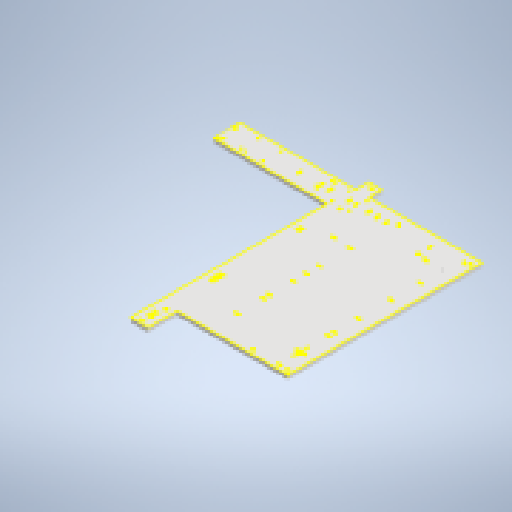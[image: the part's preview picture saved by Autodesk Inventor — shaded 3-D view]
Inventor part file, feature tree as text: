
AUTODESK INVENTOR PART (.ipt)
format: ipt  version: 2025.2 (Build 292293000, 293)  size: 1,572,352 bytes
history: native  units: in
note: dims shown in document units (in); Inventor stores cm internally (conversion verified against a paired STEP export)
features: extrude x26, other x16, sketch x11, hole x5, projected_geometry x4, move_body x3, plane x1, direct_edit x1
ambient origin geometry x8: Origin, YZ Plane, XZ Plane, XY Plane, X Axis, Y Axis, Z Axis, Center Point
bodies: Solid1 (feature_tree)
feature tree (67):
  other  "BoardMounting"
  plane  "Work Plane1"
  sketch  "Sketch2"  dims[d0=0.5in d1=0.5in]
  extrude  "Extrusion4"  Depth=0.5in
  extrude  "ForwardPathDowellPins"  Depth=0.25in
  extrude  "ReversePathDowellPins"  Depth=36.76in
  other  "CTASLMHoles"
  other  "VCSection"
  extrude  "VCPlate"  Depth=0.25in
  hole  "Hole1"  [1 undecoded]
  other  "BaseplateMountingHoles"
  extrude  "BaseplateMountingHolesInner"  Depth=3.175in
  extrude  "BaseplateMountingHolesOuter"  Depth=2.76in
  extrude  "CTASLMElementHolesTop"  Depth=2.577in
  extrude  "Extrusion10"  Depth=7.4961in
  extrude  "Extrusion11"  Depth=1.5in
  sketch  "Sketch8"  dims[d2=0.25in d3=0.4in]
  other  "CylindricalPath"
  other  "CylindricalPathOption1"
  other  "CylindricalPathOption2"
  other  "CylindricalPathOption3"
  other  "CylindricalPathOption3_CTaslmHoles"
  hole  "Hole2"  [1 undecoded]
  extrude  "Extrusion12"  Depth=0.25in
  other  "CylindricalPathOption4"
  hole  "Hole3"  [1 undecoded]
  other  "CylindricalPathOption4_CTaslmHoles"
  extrude  "Extrusion13"  Depth=0.25in
  direct_edit  "Direct Edit1"
  extrude  "CPO4_InnerHolesASLM"  Depth=0.25in
  extrude  "CPO4_InnerHolesCTASLM"  Depth=1.5in
  extrude  "CPO4_OuterHoles"  Depth=0.25in
  extrude  "CPO4_DowellPinsASLM"  Depth=1.5in
  extrude  "CPO4_DowelPinsCTASLM"  Depth=0.25in
  sketch  "Sketch22"  dims[d11=1.5in d12=0.5in]
  extrude  "Extrusion19"  Depth=0.25in
  extrude  "Extrusion20"  Depth=0.25in
  extrude  "Extrusion21"  Depth=0.5in
  extrude  "Extrusion22"  Depth=0.25in
  sketch  "Sketch24"  dims[d15=0.665in d16=2.76in]
  other  "Additional Alignment Holes Top"
  hole  "Hole4"  [1 undecoded]
  extrude  "Extrusion23"  Depth=0.25in
  extrude  "Extrusion24"  Depth=0.25in
  extrude  "Extrusion25"  Depth=0.25in
  sketch  "Sketch27"  dims[d19=10.479in d20=7.4961in]
  extrude  "Extrusion26"  Depth=0.25in
  extrude  "Extrusion27"  Depth=0.25in
  extrude  "Extrusion28"  Depth=0.25in
  hole  "Hole5"  [1 undecoded]
  sketch  "Sketch29"  dims[d23=2.0in d24=0.25in d25=0.197in d26=0.197in d27=0.0797in d28=0.0797in d29=0.25in d30=0.197in d31=0.197in d32=0.0797in d33=0.0797in d34=0.25in d35=0.197in d36=0.197in d37=0.0797in d38=0.0797in d39=0.25in d40=0.197in d41=0.197in d42=0.0797in d43=0.0797in d44=0.25in d45=0.197in d46=0.197in d47=0.0797in d48=0.0797in d49=0.25in d50=0.197in d51=0.197in d52=0.0797in d53=0.0797in d54=0.25in d55=0.197in d56=0.197in d57=0.0797in d58=0.0797in d59=0.25in d60=0.197in d61=0.197in d62=0.0797in d63=0.0797in d64=0.25in d65=0.197in d66=0.197in d67=0.08in d68=0.08in d69=0.25in d70=0.197in d71=0.197in d72=0.08in d73=0.08in d74=0.25in d75=0.197in d76=0.197in d77=0.08in d78=0.08in d81=0.175in d82=0.0in d83=1.5in d84=8.979in d85=1.5in d86=7.4961in d87=6.021in d88=1.0in d89=0.5in d90=0.4738in d91=0.4738in d92=0.25in d93=0.0797in d94=0.0797in d95=0.4738in d96=0.4738in d97=0.25in d98=0.0797in d99=0.0797in d100=0.25in d101=0.197in d102=0.197in d103=0.0797in d104=0.0797in d105=0.25in d106=0.197in d107=0.197in d108=0.0797in d109=0.0797in d110=0.25in d111=0.197in d112=0.0797in d113=0.0797in d114=0.25in d115=0.197in d116=0.0797in d117=0.0797in d118=0.5in d119=1.5in d120=0.5in d121=0.0in d122=0.75in d123=4.857in d124=9.8971in d125=6.8583in d126=1.5in d127=1.5in d128=0.5in d129=1.5in d130=0.25in d131=0.197in d132=0.197in d133=0.0797in d134=0.0797in d135=0.25in d136=0.197in d137=0.197in d138=0.0797in d139=0.0797in d140=0.25in d141=0.197in d142=0.197in d143=0.0797in d144=0.0797in d145=0.175in d146=0.0in d147=9.1809in d148=7.0827in d149=0.25in d150=0.197in d151=0.197in d152=0.0797in d153=0.0797in d154=0.25in d155=0.197in d156=0.197in d157=0.0797in d158=0.0797in d160=0.8752in d161=3.0276in d162=0.1061in d163=0.19in d164=1.5in d165=2.0in d166=1.0in d167=1.0in d168=1.0in d169=0.6in d170=0.5in d171=0.0in d172=0.196in d173=0.5in d174=0.375in d175=0.25in d176=0.5635in d177=1.0in d178=0.8108in d179=21.0in d180=27.0in d181=2.0in d182=14.0in d183=20.0in d184=2.0in d185=19.0in d186=0.4in d187=0.25in d188=0.4in d189=0.25in d190=0.4in d191=0.25in d192=0.4in d193=0.25in d194=0.4in d195=0.25in d196=0.4in d197=0.25in d198=0.4in d199=0.25in d200=0.4in d201=0.25in d202=0.4in d203=0.25in d204=0.4in d205=0.25in d206=0.5in d207=0.0in d208=0.3in d209=0.0in d210=2.0in d211=0.0in d212=0.175in d213=0.0in d214=0.4in d215=0.4in d216=0.4in d217=0.4in d218=0.4in d219=0.4in d220=0.4in d221=0.4in d222=0.4in d223=0.4in d224=0.4in d225=0.4in d226=0.4in d227=0.4in d228=0.4in d229=0.4in d230=0.4in d231=0.4in d232=0.4in d233=0.3in d234=0.0in d235=3.7433in d236=0.25in d237=0.0797in d238=0.0797in d239=0.4in d240=2.5in d241=0.75in d242=0.25in d243=0.0797in d244=0.0797in d245=1.0in d246=1.0in d247=9.1809in d248=7.0827in d249=0.25in d250=0.197in d251=0.197in d252=0.0797in d253=0.0797in d254=0.25in d255=0.197in d256=0.197in d257=0.0797in d258=0.0797in d264=0.25in d265=0.197in d266=0.197in d267=0.0797in d268=0.0797in d269=1.0in d270=1.0in d271=9.8971in d272=6.8583in d273=0.5in d274=1.5in d275=0.25in d276=0.197in d277=0.197in d278=0.0797in d279=0.0797in d280=0.25in d281=0.197in d282=0.197in d283=0.0797in d284=0.0797in d285=0.25in d286=0.197in d287=0.197in d288=0.0797in d289=0.0797in d290=1.0in d291=0.4in d292=0.4in d293=0.4in d294=0.4in d295=0.4in d296=0.4in d297=1.5in d298=0.5in d299=3.0in d300=0.6736in d301=2.7622in d302=1.5in d303=1.5in d304=3.6673in d305=6.9909in d306=1.5in d307=3.9528in d308=0.197in d309=0.197in d310=0.08in d311=0.08in d312=0.25in d313=0.197in d314=0.197in d315=0.08in d316=0.08in d317=0.25in d318=0.197in d319=0.197in d320=0.08in d321=0.08in d322=0.25in d323=0.197in d324=0.197in d325=0.08in d326=0.08in d327=0.25in d328=0.197in d329=0.197in d330=0.08in d331=0.08in d332=0.25in d333=0.197in d334=0.197in d335=0.08in d336=0.08in d337=0.25in d338=0.197in d339=0.197in d340=0.08in d341=0.08in d342=0.25in d343=0.197in d344=0.197in d345=0.08in d346=0.08in d347=0.25in d348=0.197in d349=0.197in d350=0.08in d351=0.08in d352=0.25in d353=0.197in d354=0.197in d355=0.08in d356=0.08in d357=0.25in d358=2.0in d359=0.08in d360=0.08in d361=0.25in d362=0.1509in d363=0.08in d364=0.08in d365=0.25in d366=1.5in d394=4.5in d395=2.4909in d396=0.4738in d397=0.4738in d398=0.25in d399=0.08in d400=0.08in d401=5.4909in d402=0.25in d403=1.5in d404=3.9528in d405=5.4638in d406=9.8801in d407=8.4055in d408=0.1984in d409=0.1984in d410=0.08in d411=0.08in d412=0.25in d413=0.1984in d414=0.1984in d415=0.08in d416=0.08in d417=0.25in d418=0.1984in d419=0.1984in d420=0.08in d421=0.08in d422=0.25in d423=0.4738in d424=0.4738in d425=0.25in d426=0.08in d427=0.08in d428=2.4909in d429=0.25in d430=1.5in d431=3.9528in d432=5.4638in d433=9.8801in d434=8.4055in d435=0.1984in d436=0.1984in d437=0.08in d438=0.08in d439=0.25in d440=0.1984in d441=0.1984in d442=0.08in d443=0.08in d444=0.25in d445=0.1984in d446=0.1984in d447=0.08in d448=0.08in d449=0.25in d450=1.5in d451=0.5in d452=3.0in d453=0.6736in d454=2.7622in d455=1.5in d456=1.5in d457=3.6673in d458=6.9909in d459=1.5in d460=3.9528in d461=0.197in d462=0.197in d463=0.08in d464=0.08in d465=0.25in d466=0.197in d467=0.197in d468=0.08in d469=0.08in d470=0.25in d471=0.197in d472=0.197in d473=0.08in d474=0.08in d475=0.25in d476=0.197in d477=0.197in d478=0.08in d479=0.08in d480=0.25in d481=0.197in d482=0.197in d483=0.08in d484=0.08in d485=0.25in d486=0.197in d487=0.197in d488=0.08in d489=0.08in d490=0.25in d491=0.197in d492=0.197in d493=0.08in d494=0.08in d495=0.25in d496=0.197in d497=0.197in d498=0.08in d499=0.08in d500=0.25in d501=0.197in d502=0.197in d503=0.08in d504=0.08in d505=0.25in d506=0.197in d507=0.197in d508=0.08in d509=0.08in d510=0.25in d511=2.0in d512=0.08in d513=0.08in d514=0.25in d515=0.1509in d516=0.08in d517=0.08in d518=0.25in d519=1.5in d520=4.5in d521=2.4909in d522=0.4738in d523=0.4738in d524=0.25in d525=0.08in d526=0.08in d527=2.4909in d528=0.25in d529=1.5in d530=3.9528in d531=5.4638in d532=9.8801in d533=8.4055in d534=0.1984in d535=0.1984in d536=0.08in d537=0.08in d538=0.25in d539=0.1984in d540=0.1984in d541=0.08in d542=0.08in d543=0.25in d544=0.1984in d545=0.1984in d546=0.08in d547=0.08in d548=0.25in d549=9.1634in d550=8.2568in d551=0.197in d552=0.197in d553=0.08in d554=0.08in d555=0.197in d556=0.197in d557=0.08in d558=0.08in d559=0.197in d560=0.197in d561=0.08in d562=0.08in d563=0.8752in d564=3.0276in d565=0.1061in d566=0.19in d567=1.5in d568=2.0in d569=1.0in d570=1.0in d571=1.0in d572=0.6in d573=0.196in d574=0.5in d575=0.375in d576=0.25in d577=0.5635in d578=1.0in d579=0.8108in d580=1.5in d581=0.5in d582=3.0in d583=0.5in d584=0.0in d585=1.5in d586=0.5in d587=3.0in d588=0.6736in d589=2.7622in d590=1.5in d591=1.5in d592=3.6673in d593=6.9909in d594=1.5in d595=3.9528in d596=0.197in d597=0.197in d598=0.0797in d599=0.0797in d600=0.25in d601=0.197in d602=0.197in d603=0.0797in d604=0.0797in d605=0.25in d606=0.197in d607=0.197in d608=0.0797in d609=0.0797in d610=0.25in d611=0.197in d612=0.197in d613=0.0797in d614=0.0797in d615=0.25in d616=0.197in d617=0.197in d618=0.0797in d619=0.0797in d620=0.25in d621=0.197in d622=0.197in d623=0.0797in d624=0.0797in d625=0.25in d626=0.197in d627=0.197in d628=0.0797in d629=0.0797in d630=0.25in d631=0.197in d632=0.197in d633=0.0797in d634=0.0797in d635=0.25in d636=0.197in d637=0.197in d638=0.0797in d639=0.0797in d640=0.25in d641=0.197in d642=0.197in d643=0.0797in d644=0.0797in d645=0.25in d646=2.0in d647=0.0797in d648=0.0797in d649=0.25in d650=0.1509in d651=0.0797in d652=0.0797in d653=0.25in d654=1.5in d655=4.5in d656=2.4909in d657=0.4738in d658=0.4738in d659=0.25in d660=0.0797in d661=0.0797in d662=2.4909in d663=0.25in d664=1.5in d665=3.9528in d684=0.8752in d685=3.0276in d686=0.1061in d687=0.19in d688=1.5in d689=2.0in d690=1.0in d691=1.0in d692=1.0in d693=0.6in d694=0.196in d695=0.5in d696=0.375in d697=0.25in d698=0.5635in d699=1.0in d700=0.8108in d701=0.75in d704=8.4055in d709=0.25in d714=0.25in d719=0.25in d720=9.1634in d721=8.2568in d722=0.197in d723=0.197in d724=0.0797in d725=0.0797in d726=0.197in d727=0.197in d728=0.0797in d729=0.0797in d730=0.197in d731=0.197in d732=0.0797in d733=0.0797in d734=0.5in d735=0.0in d736=0.0in d737=0.0in d738=-0.5in d739=0.0in d740=0.0in d741=-0.5in d742=0.0in d743=0.0in d744=1.0in d745=0.5in d746=0.0in d747=0.5in d748=0.0in d749=0.4in d750=0.4in d751=0.4in d752=0.4in d753=0.4in d754=0.4in d755=0.4in d756=0.4in d757=0.4in d758=0.4in d759=0.4in d760=0.4in d761=0.4in d762=0.4in d763=0.4in d764=0.4in d765=0.3in d766=0.0in d767=0.0797in d768=0.0797in d769=0.0797in d770=0.0797in d771=0.197in d772=0.0797in d773=0.175in d774=0.0in d775=0.175in d776=0.0in d777=2.5in d778=0.197in d779=0.197in d780=0.197in d781=0.197in d782=0.197in d783=0.197in d784=0.197in d785=0.197in d786=0.0797in d787=0.0797in d788=0.0797in d789=0.0797in d790=0.0797in d791=0.197in d792=0.0797in d793=0.0797in d794=0.0797in d795=0.5in d796=0.75in d797=0.75in d798=0.5in d799=0.0in d800=0.175in d801=0.0in d802=1.0in d803=0.0in d804=0.4in d805=0.3in d806=0.0in d807=0.2382in d808=0.25in d809=0.0797in d810=0.0797in d811=0.75in d812=0.25in d813=0.0797in d814=0.0797in d815=1.0in d816=0.25in d817=0.0797in d818=0.0797in d819=1.0in d820=0.25in d821=0.0797in d822=0.0797in d823=5.0in d824=0.25in d825=0.0797in d826=0.0797in d827=1.0in d828=1.0in d829=1.0in d830=2.0in d831=2.0in d832=0.196in d833=0.5in d834=0.375in d835=0.25in d836=0.5635in d837=1.0in d838=0.8108in d839=1.0in d840=0.0in d841=0.175in d842=0.0in d844=0.4in d845=0.4in d846=0.4in d847=0.4in d848=0.4in d849=0.3in d850=0.0in d853=0.5in d854=0.25in d855=0.5in d856=0.5in d857=0.5in d858=0.25in d859=0.25in d860=0.8661in d861=0.8661in d862=0.8661in d863=0.1191in d864=0.1191in d865=1.0in d866=0.0in d867=0.175in d868=0.0in d869=0.4in d870=0.4in d871=0.3in d872=0.0in d873=0.196in d874=0.5in d875=0.375in d876=0.25in d877=0.5635in d878=1.0in d879=0.8108in d880=0.1576in d881=0.25in d882=0.197in d883=0.197in d884=0.0797in d885=0.0797in d886=0.4in]
  other  "ElementHolesBottom"
  other  "CYlindricalPathOption3_VCHoles"
  sketch  "Sketch16"  dims[d4=4.0in d5=36.76in]
  other  "CylindricalPathOption4_VCHoles"
  sketch  "Sketch20"  dims[d6=0.25in d7=0.4in d8=5.0in]
  other  "MountHolesOuter_CylindricalOption4"
  projected_geometry  "Projected Loop90"
  projected_geometry  "Projected Loop92"
  projected_geometry  "Projected Loop93"
  sketch  "Sketch23"  dims[d13=2.5in d14=3.175in]
  sketch  "Sketch26"  dims[d17=7.104in d18=2.577in]
  sketch  "Sketch28"  dims[d21=1.5in d22=0.1509in]
  projected_geometry  "Projected Loop94"
  move_body  "Move1"
  move_body  "Move2"
  move_body  "Move3"
note: 5 required parameter values undecoded (feature->parameter linkage not recoverable at this tier; creation-order binding heuristic only, values carry confidence <= 0.55)
